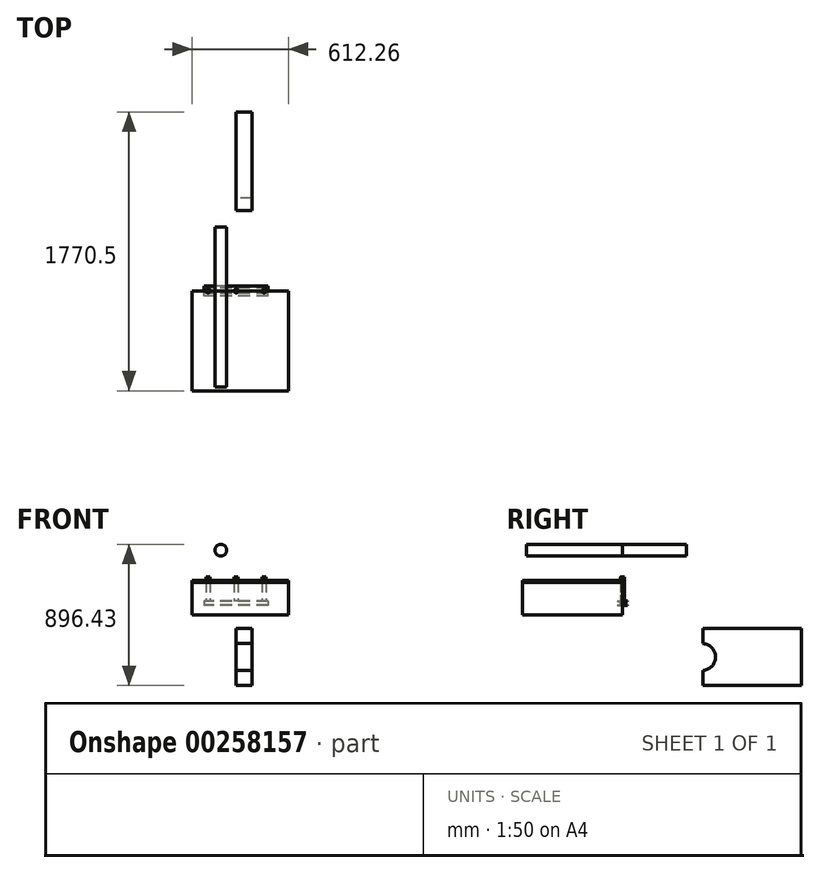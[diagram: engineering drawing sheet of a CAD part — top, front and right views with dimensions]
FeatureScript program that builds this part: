
annotation { "Feature Type Name" : "Feature", "Feature Type Description" : "" }
export const myFeature = defineFeature(function(context is Context, id is Id, definition is map)
    precondition{}
    {
        {
            var Q0;
            Q0=qCreatedBy(makeId("Top.planeOp"),FACE);
            var sketch = newSketch(context, id + "F0", { "sketchPlane" : qUnion([Q0])});
            skCircle(sketch, "E0", {"center": v(-177.8, 0) * mm, "radius": 12.7 * mm});
            skCircle(sketch, "E1", {"center": v(177.8, 0) * mm, "radius": 12.7 * mm});
            skCircle(sketch, "E2", {"center": v(0, 0) * mm, "radius": 12.7 * mm});
            skSolve(sketch);
        }
        {
            var Q0;
            Q0 = qSketchRegion(id + "F0", true);
            extrude(context, id + "F1", {"entities" : qUnion([Q0]), "depth" : 152.4 * mm});
        }
        {
            var Q0;
            Q0=qCreatedBy(makeId("Right.planeOp"),FACE);
            var sketch = newSketch(context, id + "F2", { "sketchPlane" : qUnion([Q0])});
            skLineSegment(sketch, "E3.bottom", {"start": v(-31.75, 0) * mm, "end": v(31.75, 0) * mm});
            skLineSegment(sketch, "E3.top", {"start": v(-31.75, -3.81) * mm, "end": v(31.75, -3.81) * mm});
            skLineSegment(sketch, "E3.left", {"start": v(-31.75, 0) * mm, "end": v(-31.75, -3.81) * mm});
            skLineSegment(sketch, "E3.right", {"start": v(31.75, 0) * mm, "end": v(31.75, -3.81) * mm});
            skLineSegment(sketch, "E4.bottom", {"start": v(-17.02, -3.81) * mm, "end": v(18.09, -3.81) * mm});
            skLineSegment(sketch, "E4.top", {"start": v(-17.02, -27.44) * mm, "end": v(18.09, -27.44) * mm});
            skLineSegment(sketch, "E4.left", {"start": v(-17.02, -3.81) * mm, "end": v(-17.02, -27.44) * mm});
            skLineSegment(sketch, "E4.right", {"start": v(18.09, -3.81) * mm, "end": v(18.09, -27.44) * mm});
            skLineSegment(sketch, "E5.bottom", {"start": v(-31.75, -27.23) * mm, "end": v(31.75, -27.23) * mm});
            skLineSegment(sketch, "E5.top", {"start": v(-31.75, -31.22) * mm, "end": v(31.75, -31.22) * mm});
            skLineSegment(sketch, "E5.left", {"start": v(-31.75, -27.23) * mm, "end": v(-31.75, -31.22) * mm});
            skLineSegment(sketch, "E5.right", {"start": v(31.75, -27.23) * mm, "end": v(31.75, -31.22) * mm});
            skSolve(sketch);
        }
        {
            var Q0;
            Q0 = qSketchRegion(id + "F2", true);
            extrude(context, id + "F3", {"entities" : qUnion([Q0]), "endBound" : BoundingType.SYMMETRIC, "depth" : 406.4 * mm});
        }
        {
            var Q0;
            Q0=qCreatedBy(makeId("Front.planeOp"),FACE);
            var sketch = newSketch(context, id + "F4", { "sketchPlane" : qUnion([Q0])});
            skCircle(sketch, "E6", {"center": v(-97.2, 320.7) * mm, "radius": 37.2 * mm});
            skSolve(sketch);
        }
        {
            var Q0;
            Q0=makeQuery(id+"F4.imprint","IMPRINT",FACE,{"disambiguationData":[TD([[makeQuery(id+"F4.imprint","IMPRINT",EDGE,{"derivedFrom":sQuery(id+"F4.wireOp",EDGE,"E6")}),1.0]])]});
            var Q1;
            Q1=sQuery(id+"F4.wireOp",EDGE,"E6");
            extrude(context, id + "F5", {"entities" : qUnion([Q0]), "surfaceEntities" : qUnion([Q1]), "depth" : 609.6 * mm});
        }
        {
            var Q0;
            Q0=makeQuery(id+"F5.opExtrude","CAP_FACE",FACE,{"disambiguationData":[OSD([sQuery(id+"F4.wireOp",EDGE,"E6")])],"isStart":true});
            var sketch = newSketch(context, id + "F6", { "sketchPlane" : qUnion([Q0])});
            skCircle(sketch, "E7.1", {"center": v(97.2, 320.7) * mm, "radius": 37.2 * mm});
            skSolve(sketch);
        }
        {
            var Q0;
            Q0=makeQuery(id+"F6.imprint","IMPRINT",FACE,{"disambiguationData":[TD([[makeQuery(id+"F6.imprint","IMPRINT",EDGE,{"derivedFrom":sQuery(id+"F6.wireOp",EDGE,"E7.1")}),-1.0]])]});
            extrude(context, id + "F7", {"entities" : qUnion([Q0]), "depth" : 406.4 * mm});
        }
        {
            var Q0;
            Q0=qCreatedBy(makeId("Front.planeOp"),FACE);
            var sketch = newSketch(context, id + "F8", { "sketchPlane" : qUnion([Q0])});
            skLineSegment(sketch, "E8.bottom", {"start": v(332.14, 115.16) * mm, "end": v(-280.12, 115.16) * mm});
            skLineSegment(sketch, "E8.top", {"start": v(332.14, -90.1) * mm, "end": v(-280.12, -90.1) * mm});
            skLineSegment(sketch, "E8.left", {"start": v(332.14, 115.16) * mm, "end": v(332.14, -90.1) * mm});
            skLineSegment(sketch, "E8.right", {"start": v(-280.12, 115.16) * mm, "end": v(-280.12, -90.1) * mm});
            skLineSegment(sketch, "E9.bottom", {"start": v(332.02, 128.05) * mm, "end": v(-280.12, 128.05) * mm});
            skLineSegment(sketch, "E9.top", {"start": v(332.02, 115.16) * mm, "end": v(-280.12, 115.16) * mm});
            skLineSegment(sketch, "E9.left", {"start": v(332.02, 128.05) * mm, "end": v(332.02, 115.16) * mm});
            skLineSegment(sketch, "E9.right", {"start": v(-280.12, 128.05) * mm, "end": v(-280.12, 115.16) * mm});
            skSolve(sketch);
        }
        {
            var Q0;
            Q0=makeQuery(id+"F8.imprint","IMPRINT",FACE,{"disambiguationData":[TD([[makeQuery(id+"F8.imprint","IMPRINT",EDGE,{"derivedFrom":sQuery(id+"F8.wireOp",EDGE,"E8.bottom")}),1.0]])]});
            extrude(context, id + "F9", {"entities" : qUnion([Q0]), "depth" : 635 * mm});
        }
        {
            var Q0;
            Q0=makeQuery(id+"F8.imprint","IMPRINT",FACE,{"disambiguationData":[TD([[makeQuery(id+"F8.imprint","IMPRINT",EDGE,{"derivedFrom":sQuery(id+"F8.wireOp",EDGE,"E9.bottom")}),1.0]])]});
            extrude(context, id + "F10", {"entities" : qUnion([Q0]), "depth" : 635 * mm});
        }
        {
            var Q0;
            Q0=qCreatedBy(makeId("Right.planeOp"),FACE);
            var sketch = newSketch(context, id + "F11", { "sketchPlane" : qUnion([Q0])});
            skLineSegment(sketch, "E10.bottom", {"start": v(510.27, -176.78) * mm, "end": v(1135.5, -176.78) * mm});
            skLineSegment(sketch, "E10.top", {"start": v(510.27, -538.52) * mm, "end": v(1135.5, -538.52) * mm});
            skLineSegment(sketch, "E10.left", {"start": v(510.27, -176.78) * mm, "end": v(510.27, -272.74) * mm});
            skLineSegment(sketch, "E10.right", {"start": v(1135.5, -176.78) * mm, "end": v(1135.5, -538.52) * mm});
            skArc(sketch, "E11", {"start": v(510.27, -442.56) * mm, "mid": v(590.83, -357.65) * mm, "end": v(510.27, -272.74) * mm});
            skLineSegment(sketch, "E12.trimOffspring", {"start": v(510.27, -442.56) * mm, "end": v(510.27, -538.52) * mm});
            skSolve(sketch);
        }
        {
            var Q0;
            Q0=makeQuery(id+"F11.imprint","IMPRINT",FACE,{"disambiguationData":[TD([[makeQuery(id+"F11.imprint","IMPRINT",EDGE,{"derivedFrom":sQuery(id+"F11.wireOp",EDGE,"E10.bottom")}),-1.0]])]});
            extrude(context, id + "F12", {"entities" : qUnion([Q0]), "depth" : 101.6 * mm});
        }
    });
